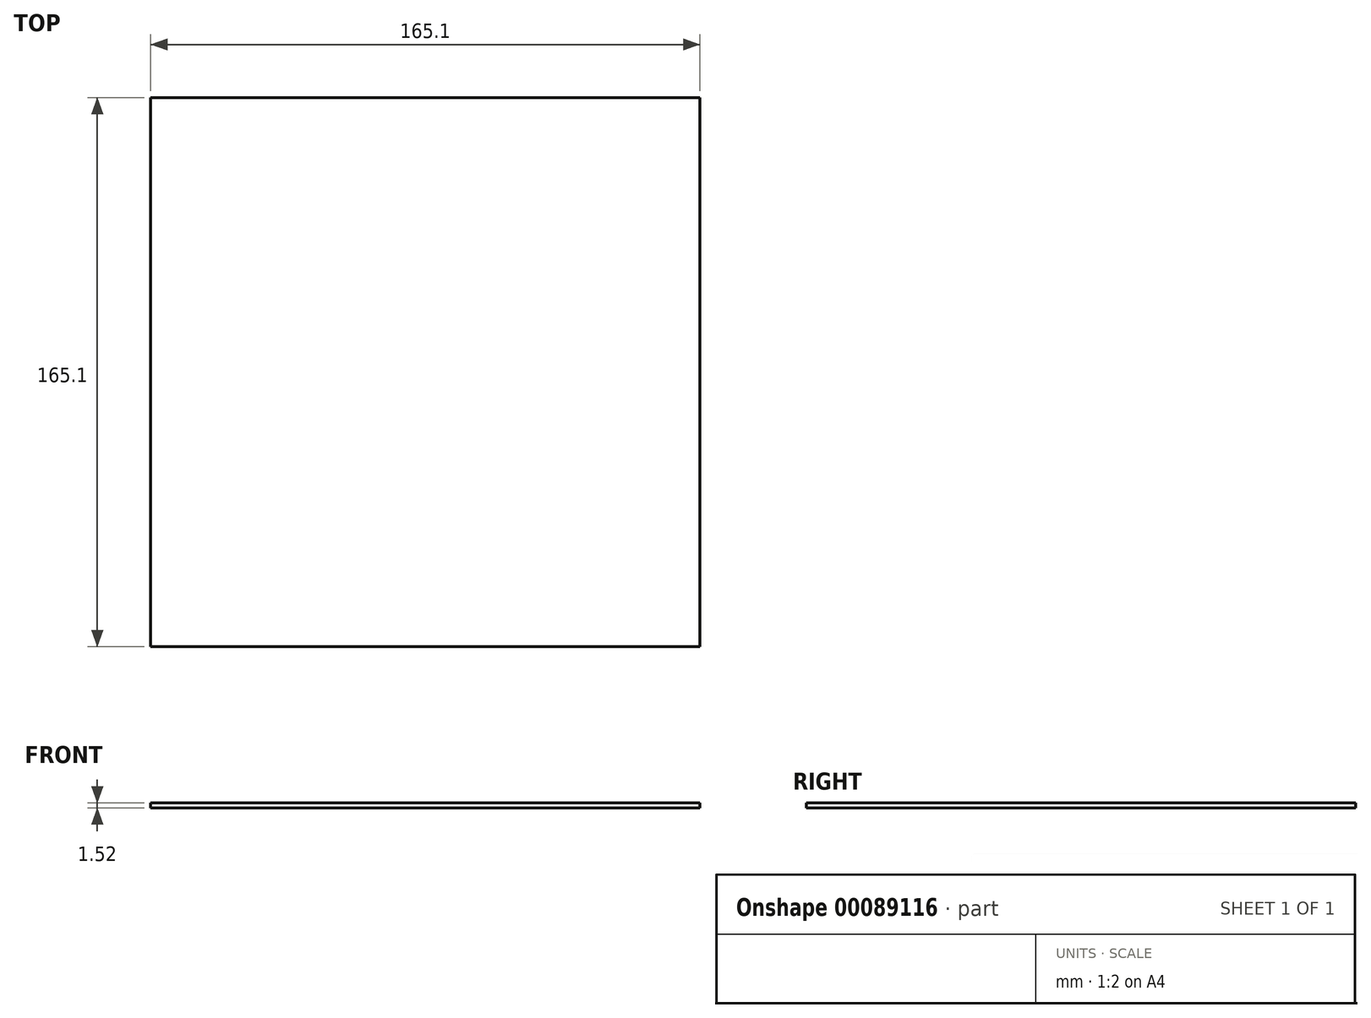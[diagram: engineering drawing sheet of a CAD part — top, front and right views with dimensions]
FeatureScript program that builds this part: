
annotation { "Feature Type Name" : "Feature", "Feature Type Description" : "" }
export const myFeature = defineFeature(function(context is Context, id is Id, definition is map)
    precondition{}
    {
        {
            var Q0;
            Q0=qCreatedBy(makeId("Top.planeOp"),FACE);
            var sketch = newSketch(context, id + "F0", { "sketchPlane" : qUnion([Q0])});
            skLineSegment(sketch, "E0.bottom", {"start": v(-80.04, 80.67) * mm, "end": v(85.06, 80.67) * mm});
            skLineSegment(sketch, "E0.top", {"start": v(-80.04, -84.43) * mm, "end": v(85.06, -84.43) * mm});
            skLineSegment(sketch, "E0.left", {"start": v(-80.04, 80.67) * mm, "end": v(-80.04, -84.43) * mm});
            skLineSegment(sketch, "E0.right", {"start": v(85.06, 80.67) * mm, "end": v(85.06, -84.43) * mm});
            skSolve(sketch);
        }
        {
            var Q0;
            Q0 = qSketchRegion(id + "F0", true);
            extrude(context, id + "F1", {"entities" : qUnion([Q0]), "depth" : 1.52 * mm});
        }
    });
